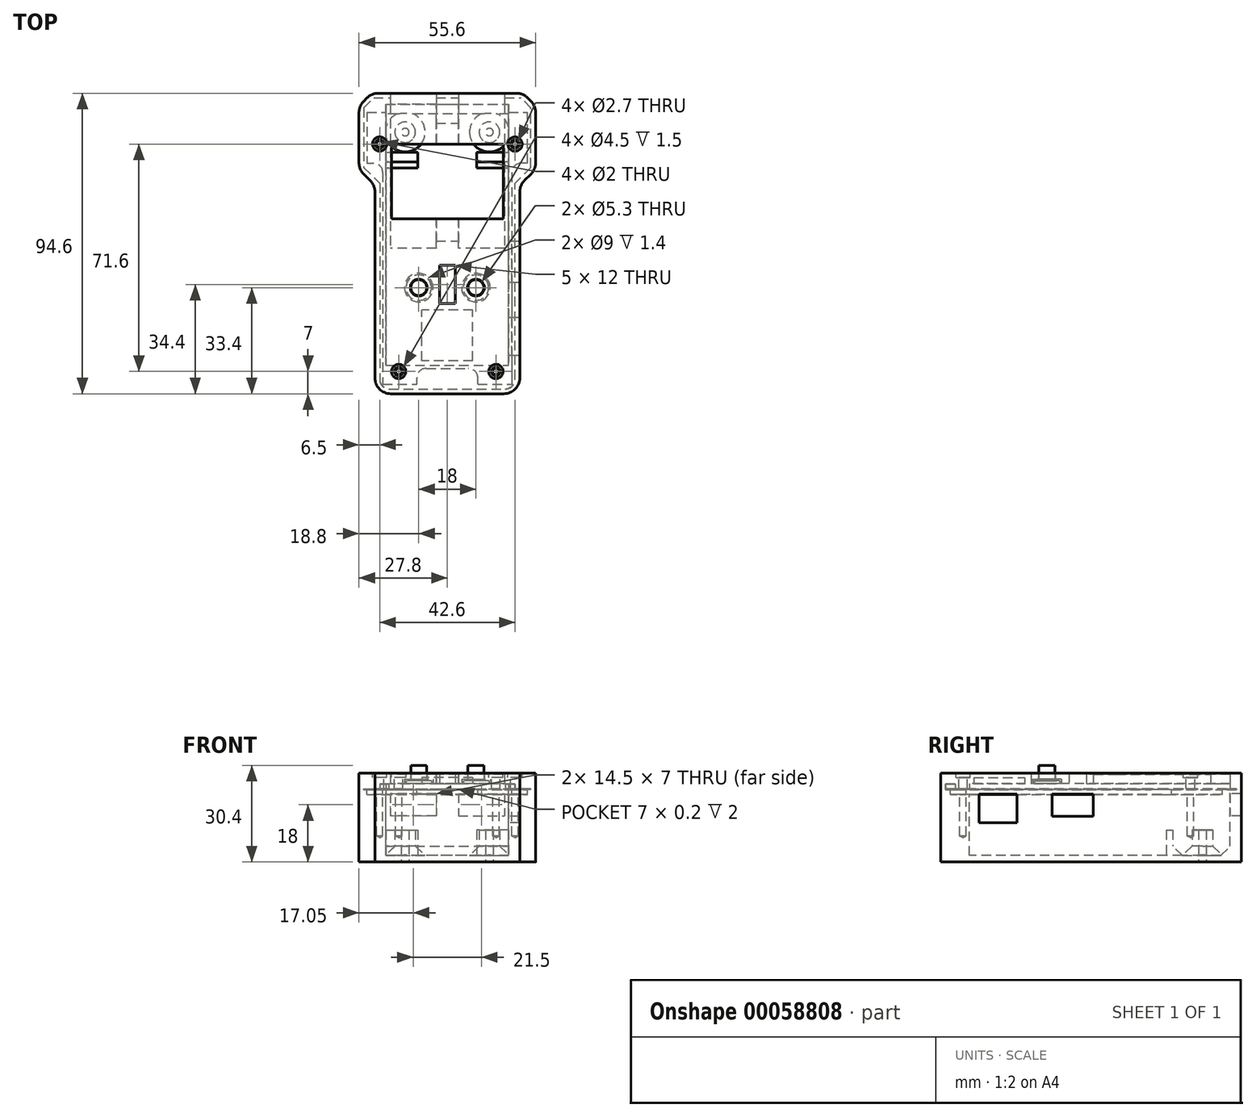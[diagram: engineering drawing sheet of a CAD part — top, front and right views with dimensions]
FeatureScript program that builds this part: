
annotation { "Feature Type Name" : "Feature", "Feature Type Description" : "" }
export const myFeature = defineFeature(function(context is Context, id is Id, definition is map)
    precondition{}
    {
        {
            assignVariable(context, id + "F0", {"name" : "GlassOffset", "anyValue" : 5.4});
        }
        {
            var Q0;
            Q0=qCreatedBy(makeId("Top.planeOp"),FACE);
            var sketch = newSketch(context, id + "F1", { "sketchPlane" : qUnion([Q0])});
            skLineSegment(sketch, "E0.rect.bottom", {"start": v(25.3, 42.8) * mm, "end": v(-25.3, 42.8) * mm, "construction": true});
            skLineSegment(sketch, "E0.rect.top", {"start": v(25.3, -42.8) * mm, "end": v(-25.3, -42.8) * mm, "construction": true});
            skLineSegment(sketch, "E0.rect.left", {"start": v(25.3, 42.8) * mm, "end": v(25.3, -42.8) * mm, "construction": true});
            skLineSegment(sketch, "E0.rect.right", {"start": v(-25.3, 42.8) * mm, "end": v(-25.3, -42.8) * mm, "construction": true});
            skPoint(sketch, "E0.rect.middle", {"position": v(0, 0) * mm});
            skLineSegment(sketch, "E1.rect.bottom", {"start": v(8, -35.4) * mm, "end": v(-8, -35.4) * mm});
            skLineSegment(sketch, "E1.rect.top", {"start": v(8, -19.4) * mm, "end": v(-8, -19.4) * mm});
            skLineSegment(sketch, "E1.rect.left", {"start": v(8, -35.4) * mm, "end": v(8, -19.4) * mm});
            skLineSegment(sketch, "E1.rect.right", {"start": v(-8, -35.4) * mm, "end": v(-8, -19.4) * mm});
            skPoint(sketch, "E1.rect.middle", {"position": v(0, -27.4) * mm});
            skPoint(sketch, "E2.rect.middle", {"position": v(0, 20.8) * mm});
            skLineSegment(sketch, "E3.rect.bottom", {"start": v(-5, -8.4) * mm, "end": v(-13, -8.4) * mm});
            skLineSegment(sketch, "E3.rect.top", {"start": v(-5, -16.4) * mm, "end": v(-13, -16.4) * mm});
            skLineSegment(sketch, "E3.rect.left", {"start": v(-5, -8.4) * mm, "end": v(-5, -16.4) * mm});
            skLineSegment(sketch, "E3.rect.right", {"start": v(-13, -8.4) * mm, "end": v(-13, -16.4) * mm});
            skPoint(sketch, "E3.rect.middle", {"position": v(-9, -12.4) * mm});
            skLineSegment(sketch, "E4.rect.bottom", {"start": v(13, -8.4) * mm, "end": v(5, -8.4) * mm});
            skLineSegment(sketch, "E4.rect.top", {"start": v(13, -16.4) * mm, "end": v(5, -16.4) * mm});
            skLineSegment(sketch, "E4.rect.left", {"start": v(13, -8.4) * mm, "end": v(13, -16.4) * mm});
            skLineSegment(sketch, "E4.rect.right", {"start": v(5, -8.4) * mm, "end": v(5, -16.4) * mm});
            skPoint(sketch, "E4.rect.middle", {"position": v(9, -12.4) * mm});
            skLineSegment(sketch, "E5", {"start": v(-9, -12.4) * mm, "end": v(9, -12.4) * mm, "construction": true});
            skLineSegment(sketch, "E6.rect.bottom", {"start": v(2.5, -5.4) * mm, "end": v(-2.5, -5.4) * mm});
            skLineSegment(sketch, "E6.rect.top", {"start": v(2.5, -17.4) * mm, "end": v(-2.5, -17.4) * mm});
            skLineSegment(sketch, "E6.rect.left", {"start": v(2.5, -5.4) * mm, "end": v(2.5, -17.4) * mm});
            skLineSegment(sketch, "E6.rect.right", {"start": v(-2.5, -5.4) * mm, "end": v(-2.5, -17.4) * mm});
            skPoint(sketch, "E6.rect.middle", {"position": v(0, -11.4) * mm});
            skCircle(sketch, "E7", {"center": v(-21.3, 32.8) * mm, "radius": 1.5 * mm});
            skCircle(sketch, "E8", {"center": v(21.3, 32.8) * mm, "radius": 1.5 * mm});
            skCircle(sketch, "E9", {"center": v(-15.3, -38.8) * mm, "radius": 1.5 * mm});
            skCircle(sketch, "E10", {"center": v(15.3, -38.8) * mm, "radius": 1.5 * mm});
            skLineSegment(sketch, "E11", {"start": v(18.3, -33.6) * mm, "end": v(18.3, -22.6) * mm, "construction": true});
            skLineSegment(sketch, "E12", {"start": v(16.3, -12.9) * mm, "end": v(16.3, 0.1) * mm, "construction": true});
            skPoint(sketch, "E13.visualSharp", {"position": v(16.3, 2.2) * mm});
            skArc(sketch, "E13.filletArc", {"start": v(17.8, 1.6) * mm, "mid": v(16.74, 1.16) * mm, "end": v(16.3, 0.1) * mm, "construction": true});
            skPoint(sketch, "E14.visualSharp", {"position": v(16.3, -10.8) * mm});
            skArc(sketch, "E14.filletArc", {"start": v(16.3, -12.9) * mm, "mid": v(16.74, -13.96) * mm, "end": v(17.8, -14.4) * mm, "construction": true});
            skPoint(sketch, "E15.visualSharp", {"position": v(18.3, -33.8) * mm});
            skArc(sketch, "E15.filletArc", {"start": v(18.3, -33.6) * mm, "mid": v(18.53, -34.17) * mm, "end": v(19.1, -34.4) * mm, "construction": true});
            skPoint(sketch, "E16.visualSharp", {"position": v(18.3, -21.8) * mm});
            skArc(sketch, "E16.filletArc", {"start": v(19.1, -21.8) * mm, "mid": v(18.53, -22.03) * mm, "end": v(18.3, -22.6) * mm, "construction": true});
            skLineSegment(sketch, "E17", {"start": v(-25.3, 42.8) * mm, "end": v(25.3, 42.8) * mm});
            skLineSegment(sketch, "E18", {"start": v(-25.3, 42.8) * mm, "end": v(-25.3, 26.8) * mm});
            skLineSegment(sketch, "E19", {"start": v(25.3, 26.8) * mm, "end": v(25.3, 42.8) * mm});
            skLineSegment(sketch, "E20", {"start": v(-25.3, 26.8) * mm, "end": v(-20.3, 26.8) * mm});
            skLineSegment(sketch, "E21", {"start": v(25.3, 26.8) * mm, "end": v(20.3, 26.8) * mm});
            skLineSegment(sketch, "E22", {"start": v(-20.3, 26.8) * mm, "end": v(-20.3, -42.8) * mm});
            skLineSegment(sketch, "E23", {"start": v(20.3, 26.8) * mm, "end": v(20.3, -42.8) * mm});
            skLineSegment(sketch, "E24", {"start": v(9.6, -42.8) * mm, "end": v(20.3, -42.8) * mm});
            skLineSegment(sketch, "E25", {"start": v(-9.6, -42.8) * mm, "end": v(-9.6, -37.8) * mm});
            skLineSegment(sketch, "E26", {"start": v(9.6, -42.8) * mm, "end": v(9.6, -37.8) * mm});
            skLineSegment(sketch, "E27", {"start": v(-20.3, -42.8) * mm, "end": v(-9.6, -42.8) * mm});
            skLineSegment(sketch, "E28", {"start": v(-9.6, -37.8) * mm, "end": v(9.6, -37.8) * mm});
            skLineSegment(sketch, "E29.rect.bottom", {"start": v(17.8, 39.3) * mm, "end": v(-17.8, 39.3) * mm});
            skLineSegment(sketch, "E29.rect.top", {"start": v(17.8, 2.3) * mm, "end": v(-17.8, 2.3) * mm});
            skLineSegment(sketch, "E29.rect.left", {"start": v(17.8, 39.3) * mm, "end": v(17.8, 2.3) * mm});
            skLineSegment(sketch, "E29.rect.right", {"start": v(-17.8, 39.3) * mm, "end": v(-17.8, 2.3) * mm});
            skLineSegment(sketch, "E30.rect.bottom", {"start": v(17.6, 9.3) * mm, "end": v(-17.6, 9.3) * mm});
            skLineSegment(sketch, "E30.rect.top", {"start": v(17.6, 32.8) * mm, "end": v(-17.6, 32.8) * mm});
            skLineSegment(sketch, "E30.rect.left", {"start": v(17.6, 9.3) * mm, "end": v(17.6, 32.8) * mm});
            skLineSegment(sketch, "E30.rect.right", {"start": v(-17.6, 9.3) * mm, "end": v(-17.6, 32.8) * mm});
            skPoint(sketch, "E30.rect.middle", {"position": v(0, 21.05) * mm});
            skLineSegment(sketch, "E31", {"start": v(0, 0) * mm, "end": v(0, 42.8) * mm, "construction": true});
            skLineSegment(sketch, "E32", {"start": v(0, 0) * mm, "end": v(0, -12.4) * mm, "construction": true});
            skCircle(sketch, "E33", {"center": v(-21.3, 32.8) * mm, "radius": 3 * mm});
            skCircle(sketch, "E34", {"center": v(21.3, 32.8) * mm, "radius": 3 * mm});
            skCircle(sketch, "E35", {"center": v(15.3, -38.8) * mm, "radius": 3 * mm});
            skCircle(sketch, "E36", {"center": v(-15.3, -38.8) * mm, "radius": 3 * mm});
            skLineSegment(sketch, "E37.MirrorCS", {"start": v(18.9, 40.8) * mm, "end": v(3.9, 40.8) * mm, "construction": true});
            skSolve(sketch);
        }
        {
            var Q0;
            Q0=qCreatedBy(makeId("Top.planeOp"),FACE);
            var sketch = newSketch(context, id + "F2", { "sketchPlane" : qUnion([Q0])});
            skPoint(sketch, "E38.0", {"position": v(-9, -12.4) * mm});
            skPoint(sketch, "E39.0", {"position": v(9, -12.4) * mm});
            skCircle(sketch, "E40", {"center": v(-9, -12.4) * mm, "radius": 4 * mm});
            skCircle(sketch, "E41", {"center": v(9, -12.4) * mm, "radius": 4 * mm});
            skCircle(sketch, "E42", {"center": v(-9, -12.4) * mm, "radius": 2.5 * mm});
            skCircle(sketch, "E43", {"center": v(9, -12.4) * mm, "radius": 2.5 * mm});
            skSolve(sketch);
        }
        {
            var Q0;
            Q0=qCreatedBy(makeId("Top.planeOp"),FACE);
            var sketch = newSketch(context, id + "F3", { "sketchPlane" : qUnion([Q0])});
            skLineSegment(sketch, "E44", {"start": v(-22.8, -45.8) * mm, "end": v(22.8, -45.8) * mm});
            skLineSegment(sketch, "E45", {"start": v(-27.8, 24.8) * mm, "end": v(-22.8, 19.8) * mm});
            skLineSegment(sketch, "E46", {"start": v(-22.8, 19.8) * mm, "end": v(-22.8, -45.8) * mm});
            skLineSegment(sketch, "E47", {"start": v(27.8, 24.8) * mm, "end": v(22.8, 19.8) * mm});
            skLineSegment(sketch, "E48", {"start": v(22.8, -45.8) * mm, "end": v(22.8, 19.8) * mm});
            skLineSegment(sketch, "E49", {"start": v(-27.8, 44.8) * mm, "end": v(-23.8, 48.8) * mm});
            skLineSegment(sketch, "E50", {"start": v(27.8, 44.8) * mm, "end": v(23.8, 48.8) * mm});
            skLineSegment(sketch, "E51", {"start": v(-27.8, 44.8) * mm, "end": v(-27.8, 24.8) * mm});
            skLineSegment(sketch, "E52", {"start": v(27.8, 24.8) * mm, "end": v(27.8, 44.8) * mm});
            skLineSegment(sketch, "E53", {"start": v(-23.8, 48.8) * mm, "end": v(23.8, 48.8) * mm});
            skLineSegment(sketch, "E54.0", {"start": v(-26.3, 44.18) * mm, "end": v(-23.18, 47.3) * mm});
            skLineSegment(sketch, "E54.1", {"start": v(-23.18, 47.3) * mm, "end": v(23.18, 47.3) * mm});
            skLineSegment(sketch, "E54.2", {"start": v(-26.3, 44.18) * mm, "end": v(-26.3, 25.42) * mm});
            skLineSegment(sketch, "E54.3", {"start": v(26.3, 44.18) * mm, "end": v(23.18, 47.3) * mm});
            skLineSegment(sketch, "E54.4", {"start": v(26.3, 25.42) * mm, "end": v(26.3, 44.18) * mm});
            skLineSegment(sketch, "E54.5", {"start": v(26.3, 25.42) * mm, "end": v(21.3, 20.42) * mm});
            skLineSegment(sketch, "E54.6", {"start": v(-26.3, 25.42) * mm, "end": v(-21.3, 20.42) * mm});
            skLineSegment(sketch, "E54.7", {"start": v(-21.3, 20.42) * mm, "end": v(-21.3, -44.3) * mm});
            skLineSegment(sketch, "E54.8", {"start": v(-21.3, -44.3) * mm, "end": v(21.3, -44.3) * mm});
            skLineSegment(sketch, "E54.9", {"start": v(21.3, -44.3) * mm, "end": v(21.3, 20.42) * mm});
            skLineSegment(sketch, "E55", {"start": v(-19.3, -36.8) * mm, "end": v(19.3, -36.8) * mm});
            skLineSegment(sketch, "E56", {"start": v(-19.3, -36.8) * mm, "end": v(-19.3, 45.3) * mm});
            skLineSegment(sketch, "E57", {"start": v(-19.3, 45.3) * mm, "end": v(19.3, 45.3) * mm});
            skLineSegment(sketch, "E58", {"start": v(19.3, 45.3) * mm, "end": v(19.3, -36.8) * mm});
            skSolve(sketch);
        }
        {
            var Q0;
            Q0=qCreatedBy(makeId("Front.planeOp"),FACE);
            var sketch = newSketch(context, id + "F4", { "sketchPlane" : qUnion([Q0])});
            skLineSegment(sketch, "E59.bottom", {"start": v(-3.5, -1.5) * mm, "end": v(-18, -1.5) * mm});
            skLineSegment(sketch, "E59.top", {"start": v(-3.5, -8.5) * mm, "end": v(-18, -8.5) * mm});
            skLineSegment(sketch, "E59.left", {"start": v(-3.5, -1.5) * mm, "end": v(-3.5, -8.5) * mm});
            skLineSegment(sketch, "E59.right", {"start": v(-18, -1.5) * mm, "end": v(-18, -8.5) * mm});
            skLineSegment(sketch, "E60.MirrorCS", {"start": v(3.5, -1.5) * mm, "end": v(18, -1.5) * mm});
            skLineSegment(sketch, "E61.MirrorCS", {"start": v(18, -1.5) * mm, "end": v(18, -8.5) * mm});
            skLineSegment(sketch, "E62.MirrorCS", {"start": v(3.5, -8.5) * mm, "end": v(18, -8.5) * mm});
            skLineSegment(sketch, "E63.MirrorCS", {"start": v(3.5, -1.5) * mm, "end": v(3.5, -8.5) * mm});
            skLineSegment(sketch, "E64", {"start": v(-3.5, -1.5) * mm, "end": v(-3.5, 4.64) * mm});
            skLineSegment(sketch, "E65", {"start": v(-3.5, 4.64) * mm, "end": v(-18, 4.64) * mm});
            skLineSegment(sketch, "E66", {"start": v(-18, 4.64) * mm, "end": v(-18, -1.5) * mm});
            skLineSegment(sketch, "E67", {"start": v(18, -1.5) * mm, "end": v(18, 4.64) * mm});
            skLineSegment(sketch, "E68", {"start": v(18, 4.64) * mm, "end": v(3.5, 4.64) * mm});
            skLineSegment(sketch, "E69", {"start": v(3.5, 4.64) * mm, "end": v(3.5, -1.5) * mm});
            skSolve(sketch);
        }
        {
            var Q0;
            Q0=qCreatedBy(makeId("Right.planeOp"),FACE);
            var sketch = newSketch(context, id + "F5", { "sketchPlane" : qUnion([Q0])});
            skLineSegment(sketch, "E70.bottom", {"start": v(-33.8, -1.6) * mm, "end": v(-21.8, -1.6) * mm});
            skLineSegment(sketch, "E70.top", {"start": v(-33.8, -10.6) * mm, "end": v(-21.8, -10.6) * mm});
            skLineSegment(sketch, "E70.left", {"start": v(-33.8, -1.6) * mm, "end": v(-33.8, -10.6) * mm});
            skLineSegment(sketch, "E70.right", {"start": v(-21.8, -1.6) * mm, "end": v(-21.8, -10.6) * mm});
            skLineSegment(sketch, "E71.bottom", {"start": v(-10.8, -1.6) * mm, "end": v(2.2, -1.6) * mm});
            skLineSegment(sketch, "E71.top", {"start": v(-10.8, -8.6) * mm, "end": v(2.2, -8.6) * mm});
            skLineSegment(sketch, "E71.left", {"start": v(-10.8, -1.6) * mm, "end": v(-10.8, -8.6) * mm});
            skLineSegment(sketch, "E71.right", {"start": v(2.2, -1.6) * mm, "end": v(2.2, -8.6) * mm});
            skPoint(sketch, "E72.0", {"position": v(-33.8, 0) * mm});
            skPoint(sketch, "E73.0", {"position": v(-21.8, 0) * mm});
            skPoint(sketch, "E74.0", {"position": v(-10.8, 0) * mm});
            skPoint(sketch, "E75.0", {"position": v(2.2, 0) * mm});
            skSolve(sketch);
        }
        {
            var Q0;
            Q0=makeQuery(id+"F3.imprint","IMPRINT",FACE,{"disambiguationData":[TD([[makeQuery(id+"F3.imprint","IMPRINT",EDGE,{"derivedFrom":sQuery(id+"F3.wireOp",EDGE,"daaaa8a0-0a0e-469a-a0b3-6c36c1fbd0ea.6")}),1.0]])]});
            var Q1;
            Q1=makeQuery(id+"F3.imprint","IMPRINT",FACE,{"disambiguationData":[TD([[makeQuery(id+"F3.imprint","IMPRINT",EDGE,{"derivedFrom":sQuery(id+"F3.wireOp",EDGE,"E44")}),1.0]])]});
            var Q2;
            Q2=makeQuery(id+"F3.imprint","IMPRINT",FACE,{"disambiguationData":[TD([[makeQuery(id+"F3.imprint","IMPRINT",EDGE,{"derivedFrom":sQuery(id+"F3.wireOp",EDGE,"E54.0")}),-1.0]])]});
            var Q3;
            Q3=makeQuery(id+"F3.imprint","IMPRINT",FACE,{"disambiguationData":[TD([[makeQuery(id+"F3.imprint","IMPRINT",EDGE,{"derivedFrom":sQuery(id+"F3.wireOp",EDGE,"E55")}),1.0]])]});
            extrude(context, id + "F6", {"entities" : qUnion([Q0, Q1, Q2, Q3]), "depth" : 5 * mm});
        }
        {
            var Q0;
            Q0=makeQuery(id+"F3.imprint","IMPRINT",FACE,{"disambiguationData":[TD([[makeQuery(id+"F3.imprint","IMPRINT",EDGE,{"derivedFrom":sQuery(id+"F3.wireOp",EDGE,"E44")}),1.0]])]});
            extrude(context, id + "F7", {"entities" : qUnion([Q0]), "operationType" : NewBodyOperationType.REMOVE, "depth" : 1.5 * mm});
        }
        {
            var Q0;
            Q0=makeQuery(id+"F3.imprint","IMPRINT",FACE,{"disambiguationData":[TD([[makeQuery(id+"F3.imprint","IMPRINT",EDGE,{"derivedFrom":sQuery(id+"F3.wireOp",EDGE,"E44")}),1.0]])]});
            extrude(context, id + "F8", {"entities" : qUnion([Q0]), "oppositeDirection" : true, "depth" : 23 * mm, "hasSecondDirection" : true, "secondDirectionOppositeDirection" : false, "secondDirectionDepth" : 1.5 * mm});
        }
        {
            var Q0;
            Q0=makeQuery(id+"F3.imprint","IMPRINT",FACE,{"disambiguationData":[TD([[makeQuery(id+"F3.imprint","IMPRINT",EDGE,{"derivedFrom":sQuery(id+"F3.wireOp",EDGE,"E54.0")}),-1.0]])]});
            var Q1;
            Q1=makeQuery(id+"F8.opExtrude","CAP_FACE",FACE,{"disambiguationData":[OSD([sQuery(id+"F3.wireOp",EDGE,"E44"),sQuery(id+"F3.wireOp",EDGE,"E45"),sQuery(id+"F3.wireOp",EDGE,"E46"),sQuery(id+"F3.wireOp",EDGE,"E47"),sQuery(id+"F3.wireOp",EDGE,"E48"),sQuery(id+"F3.wireOp",EDGE,"E49"),sQuery(id+"F3.wireOp",EDGE,"E50"),sQuery(id+"F3.wireOp",EDGE,"E51"),sQuery(id+"F3.wireOp",EDGE,"E52"),sQuery(id+"F3.wireOp",EDGE,"E53"),sQuery(id+"F3.wireOp",EDGE,"E54.0"),sQuery(id+"F3.wireOp",EDGE,"E54.1"),sQuery(id+"F3.wireOp",EDGE,"E54.2"),sQuery(id+"F3.wireOp",EDGE,"E54.3"),sQuery(id+"F3.wireOp",EDGE,"E54.4"),sQuery(id+"F3.wireOp",EDGE,"E54.5"),sQuery(id+"F3.wireOp",EDGE,"E54.6"),sQuery(id+"F3.wireOp",EDGE,"E54.7"),sQuery(id+"F3.wireOp",EDGE,"E54.8"),sQuery(id+"F3.wireOp",EDGE,"E54.9")])],"isStart":false});
            extrude(context, id + "F9", {"entities" : qUnion([Q0]), "operationType" : NewBodyOperationType.ADD, "endBound" : BoundingType.UP_TO_SURFACE, "oppositeDirection" : true, "endBoundEntityFace" : qUnion([Q1]), "depth" : 5 * mm, "hasSecondDirection" : true, "secondDirectionOppositeDirection" : true, "secondDirectionDepth" : .2 * mm});
        }
        {
            var Q0;
            Q0=makeQuery(id+"F1.imprint","IMPRINT",FACE,{"disambiguationData":[TD([[makeQuery(id+"F1.imprint","IMPRINT",EDGE,{"derivedFrom":sQuery(id+"F1.wireOp",EDGE,"E30.rect.bottom")}),-1.0]])]});
            var Q1;
            Q1=makeQuery(id+"F1.imprint","IMPRINT",FACE,{"disambiguationData":[TD([[makeQuery(id+"F1.imprint","IMPRINT",EDGE,{"derivedFrom":sQuery(id+"F1.wireOp",EDGE,"E6.rect.bottom")}),1.0]])]});
            extrude(context, id + "F10", {"entities" : qUnion([Q0, Q1]), "operationType" : NewBodyOperationType.REMOVE, "depth" : 25 * mm});
        }
        {
            var Q0;
            Q0=sQuery(id+"F1.wireOp",VERTEX,"E3.rect.middle");
            var Q1;
            Q1=sQuery(id+"F1.wireOp",VERTEX,"E4.rect.middle");
            var Q2;
            Q2=makeQuery(id+"F6.opExtrude","SWEPT_BODY",BODY,{"disambiguationData":[OSD([sQuery(id+"F3.wireOp",EDGE,"E44"),sQuery(id+"F3.wireOp",EDGE,"E45"),sQuery(id+"F3.wireOp",EDGE,"E46"),sQuery(id+"F3.wireOp",EDGE,"E47"),sQuery(id+"F3.wireOp",EDGE,"E48"),sQuery(id+"F3.wireOp",EDGE,"E49"),sQuery(id+"F3.wireOp",EDGE,"E50"),sQuery(id+"F3.wireOp",EDGE,"E51"),sQuery(id+"F3.wireOp",EDGE,"E52"),sQuery(id+"F3.wireOp",EDGE,"E53"),sQuery(id+"F3.wireOp",EDGE,"E55"),sQuery(id+"F3.wireOp",EDGE,"E56"),sQuery(id+"F3.wireOp",EDGE,"E57"),sQuery(id+"F3.wireOp",EDGE,"E58")])]});
            hole(context, id + "F11", {"style" : HoleStyle.C_BORE, "endStyle" : HoleEndStyle.BLIND, "oppositeDirection" : true, "holeDiameter" : 5.3 * mm, "cBoreDiameter" : 9 * mm, "cBoreDepth" : 3.1 * mm, "holeDepth" : 7 * mm, "locations" : qUnion([Q0, Q1]), "scope" : qUnion([Q2])});
        }
        {
            var Q0;
            Q0 = qSketchRegion(id + "F2", true);
            extrude(context, id + "F12", {"entities" : qUnion([Q0]), "depth" : 2.6 * mm, "hasSecondDirection" : true, "secondDirectionOppositeDirection" : false, "secondDirectionDepth" : 1.6 * mm});
        }
        {
            var Q0;
            Q0=makeQuery(id+"F2.imprint","IMPRINT",FACE,{"disambiguationData":[TD([[makeQuery(id+"F2.imprint","IMPRINT",EDGE,{"derivedFrom":sQuery(id+"F2.wireOp",EDGE,"E42")}),1.0]])]});
            var Q1;
            Q1=makeQuery(id+"F2.imprint","IMPRINT",FACE,{"disambiguationData":[TD([[makeQuery(id+"F2.imprint","IMPRINT",EDGE,{"derivedFrom":sQuery(id+"F2.wireOp",EDGE,"E43")}),1.0]])]});
            var Q2;
            Q2=sQuery(id+"F2.wireOp",EDGE,"E42");
            var Q3;
            Q3=sQuery(id+"F2.wireOp",EDGE,"E43");
            extrude(context, id + "F13", {"entities" : qUnion([Q0, Q1]), "operationType" : NewBodyOperationType.ADD, "surfaceEntities" : qUnion([Q2, Q3]), "depth" : (getVariable(context, 'GlassOffset') + 2) * mm, "hasSecondDirection" : true, "secondDirectionOppositeDirection" : false, "secondDirectionDepth" : 1.6 * mm});
        }
        {
            var Q0;
            Q0=makeQuery(id+"F1.imprint","IMPRINT",FACE,{"disambiguationData":[TD([[makeQuery(id+"F1.imprint","IMPRINT",EDGE,{"derivedFrom":sQuery(id+"F1.wireOp",EDGE,"E1.rect.bottom")}),1.0]])]});
            var Q1;
            Q1=makeQuery(id+"F1.imprint","IMPRINT",FACE,{"disambiguationData":[TD([[makeQuery(id+"F1.imprint","IMPRINT",EDGE,{"derivedFrom":sQuery(id+"F1.wireOp",EDGE,"E7")}),-1.0]])]});
            var Q2;
            Q2=makeQuery(id+"F1.imprint","IMPRINT",FACE,{"disambiguationData":[TD([[makeQuery(id+"F1.imprint","IMPRINT",EDGE,{"derivedFrom":sQuery(id+"F1.wireOp",EDGE,"E7")}),1.0]])]});
            var Q3;
            Q3=makeQuery(id+"F1.imprint","IMPRINT",FACE,{"disambiguationData":[TD([[makeQuery(id+"F1.imprint","IMPRINT",EDGE,{"derivedFrom":sQuery(id+"F1.wireOp",EDGE,"E8")}),-1.0]])]});
            var Q4;
            Q4=makeQuery(id+"F1.imprint","IMPRINT",FACE,{"disambiguationData":[TD([[makeQuery(id+"F1.imprint","IMPRINT",EDGE,{"derivedFrom":sQuery(id+"F1.wireOp",EDGE,"E8")}),1.0]])]});
            var Q5;
            Q5=makeQuery(id+"F1.imprint","IMPRINT",FACE,{"disambiguationData":[TD([[makeQuery(id+"F1.imprint","IMPRINT",EDGE,{"derivedFrom":sQuery(id+"F1.wireOp",EDGE,"E10")}),-1.0]])]});
            var Q6;
            Q6=makeQuery(id+"F1.imprint","IMPRINT",FACE,{"disambiguationData":[TD([[makeQuery(id+"F1.imprint","IMPRINT",EDGE,{"derivedFrom":sQuery(id+"F1.wireOp",EDGE,"E10")}),1.0]])]});
            var Q7;
            Q7=makeQuery(id+"F1.imprint","IMPRINT",FACE,{"disambiguationData":[TD([[makeQuery(id+"F1.imprint","IMPRINT",EDGE,{"derivedFrom":sQuery(id+"F1.wireOp",EDGE,"E9")}),-1.0]])]});
            var Q8;
            Q8=makeQuery(id+"F1.imprint","IMPRINT",FACE,{"disambiguationData":[TD([[makeQuery(id+"F1.imprint","IMPRINT",EDGE,{"derivedFrom":sQuery(id+"F1.wireOp",EDGE,"E9")}),1.0]])]});
            extrude(context, id + "F14", {"entities" : qUnion([Q0, Q1, Q2, Q3, Q4, Q5, Q6, Q7, Q8]), "operationType" : NewBodyOperationType.REMOVE, "oppositeDirection" : true, "depth" : 1.8 * mm});
        }
        {
            var Q0;
            Q0=makeQuery(id+"F14.boolean.opBoolean","COPY",EDGE,{"derivedFrom":makeQuery(id+"F14.opExtrude","SWEPT_EDGE",EDGE,{"disambiguationData":[OSD([sQuery(id+"F1.wireOp",EDGE,"E21"),sQuery(id+"F1.wireOp",EDGE,"E23")])]})});
            var Q1;
            Q1=makeQuery(id+"F14.boolean.opBoolean","COPY",EDGE,{"derivedFrom":makeQuery(id+"F14.opExtrude","SWEPT_EDGE",EDGE,{"disambiguationData":[OSD([sQuery(id+"F1.wireOp",EDGE,"E26"),sQuery(id+"F1.wireOp",EDGE,"E28")])]})});
            var Q2;
            Q2=makeQuery(id+"F14.boolean.opBoolean","COPY",EDGE,{"derivedFrom":makeQuery(id+"F14.opExtrude","SWEPT_EDGE",EDGE,{"disambiguationData":[OSD([sQuery(id+"F1.wireOp",EDGE,"E25"),sQuery(id+"F1.wireOp",EDGE,"E28")])]})});
            var Q3;
            Q3=makeQuery(id+"F14.boolean.opBoolean","COPY",EDGE,{"derivedFrom":makeQuery(id+"F14.opExtrude","SWEPT_EDGE",EDGE,{"disambiguationData":[OSD([sQuery(id+"F1.wireOp",EDGE,"E20"),sQuery(id+"F1.wireOp",EDGE,"E22")])]})});
            fillet(context, id + "F15", {"entities" : qUnion([Q0, Q1, Q2, Q3]), "radius" : 3 * mm, "tangentPropagation" : true, "allowEdgeOverflow" : false});
        }
        {
            var Q0;
            Q0=makeQuery(id+"F4.imprint","IMPRINT",FACE,{"disambiguationData":[TD([[makeQuery(id+"F4.imprint","IMPRINT",EDGE,{"derivedFrom":sQuery(id+"F4.wireOp",EDGE,"E59.bottom")}),1.0]])]});
            var Q1;
            Q1=makeQuery(id+"F4.imprint","IMPRINT",FACE,{"disambiguationData":[TD([[makeQuery(id+"F4.imprint","IMPRINT",EDGE,{"derivedFrom":sQuery(id+"F4.wireOp",EDGE,"E60.MirrorCS")}),-1.0]])]});
            var Q2;
            Q2=makeQuery(id+"F4.imprint","IMPRINT",FACE,{"disambiguationData":[TD([[makeQuery(id+"F4.imprint","IMPRINT",EDGE,{"derivedFrom":sQuery(id+"F4.wireOp",EDGE,"E60.MirrorCS")}),1.0]])]});
            var Q3;
            Q3=makeQuery(id+"F4.imprint","IMPRINT",FACE,{"disambiguationData":[TD([[makeQuery(id+"F4.imprint","IMPRINT",EDGE,{"derivedFrom":sQuery(id+"F4.wireOp",EDGE,"E59.bottom")}),-1.0]])]});
            extrude(context, id + "F16", {"entities" : qUnion([Q0, Q1, Q2, Q3]), "operationType" : NewBodyOperationType.REMOVE, "oppositeDirection" : true, "depth" : 50 * mm});
        }
        {
            var Q0;
            Q0=makeQuery(id+"F5.imprint","IMPRINT",FACE,{"disambiguationData":[TD([[makeQuery(id+"F5.imprint","IMPRINT",EDGE,{"derivedFrom":sQuery(id+"F5.wireOp",EDGE,"E70.bottom")}),-1.0]])]});
            var Q1;
            Q1=makeQuery(id+"F5.imprint","IMPRINT",FACE,{"disambiguationData":[TD([[makeQuery(id+"F5.imprint","IMPRINT",EDGE,{"derivedFrom":sQuery(id+"F5.wireOp",EDGE,"E71.bottom")}),-1.0]])]});
            extrude(context, id + "F17", {"entities" : qUnion([Q0, Q1]), "operationType" : NewBodyOperationType.REMOVE, "depth" : 25 * mm});
        }
        {
            var Q0;
            Q0=makeQuery(id+"F3.imprint","IMPRINT",FACE,{"disambiguationData":[TD([[makeQuery(id+"F3.imprint","IMPRINT",EDGE,{"derivedFrom":sQuery(id+"F3.wireOp",EDGE,"E44")}),1.0]])]});
            var Q1;
            Q1=makeQuery(id+"F3.imprint","IMPRINT",FACE,{"disambiguationData":[TD([[makeQuery(id+"F3.imprint","IMPRINT",EDGE,{"derivedFrom":sQuery(id+"F3.wireOp",EDGE,"E54.0")}),-1.0]])]});
            var Q2;
            Q2=makeQuery(id+"F3.imprint","IMPRINT",FACE,{"disambiguationData":[TD([[makeQuery(id+"F3.imprint","IMPRINT",EDGE,{"derivedFrom":sQuery(id+"F3.wireOp",EDGE,"E55")}),1.0]])]});
            var Q3;
            {var subQ0=sQuery(id+"F3.wireOp",EDGE,"E54.9");var subQ1=sQuery(id+"F3.wireOp",EDGE,"E54.8");var subQ2=sQuery(id+"F3.wireOp",EDGE,"E54.7");var subQ3=sQuery(id+"F3.wireOp",EDGE,"E54.6");var subQ4=sQuery(id+"F3.wireOp",EDGE,"E54.5");var subQ5=sQuery(id+"F3.wireOp",EDGE,"E54.4");var subQ6=sQuery(id+"F3.wireOp",EDGE,"E54.3");var subQ7=sQuery(id+"F3.wireOp",EDGE,"E54.2");var subQ8=sQuery(id+"F3.wireOp",EDGE,"E54.1");var subQ9=sQuery(id+"F3.wireOp",EDGE,"E54.0");var subQ10=sQuery(id+"F3.wireOp",EDGE,"E53");var subQ11=sQuery(id+"F3.wireOp",EDGE,"E52");var subQ12=sQuery(id+"F3.wireOp",EDGE,"E51");var subQ13=sQuery(id+"F3.wireOp",EDGE,"E50");var subQ14=sQuery(id+"F3.wireOp",EDGE,"E49");var subQ15=sQuery(id+"F3.wireOp",EDGE,"E48");var subQ16=sQuery(id+"F3.wireOp",EDGE,"E47");var subQ17=sQuery(id+"F3.wireOp",EDGE,"E46");var subQ18=sQuery(id+"F3.wireOp",EDGE,"E45");var subQ19=sQuery(id+"F3.wireOp",EDGE,"E44");Q3=makeQuery(id+"F9.boolean.opBoolean","MERGE",FACE,{"derivedFrom":[makeQuery(id+"F8.opExtrude","CAP_FACE",FACE,{"disambiguationData":[OSD([subQ19,subQ18,subQ17,subQ16,subQ15,subQ14,subQ13,subQ12,subQ11,subQ10,subQ9,subQ8,subQ7,subQ6,subQ5,subQ4,subQ3,subQ2,subQ1,subQ0])],"isStart":false}),makeQuery(id+"F9.opExtrude","CAP_FACE",FACE,{"disambiguationData":[OSD([subQ19,subQ18,subQ17,subQ16,subQ15,subQ14,subQ13,subQ12,subQ11,subQ10,subQ9,subQ8,subQ7,subQ6,subQ5,subQ4,subQ3,subQ2,subQ1,subQ0])],"isStart":false})]});}
            extrude(context, id + "F18", {"entities" : qUnion([Q0, Q1, Q2]), "operationType" : NewBodyOperationType.ADD, "endBound" : BoundingType.UP_TO_SURFACE, "oppositeDirection" : true, "endBoundEntityFace" : qUnion([Q3]), "depth" : 25 * mm, "hasSecondDirection" : true, "secondDirectionOppositeDirection" : true, "secondDirectionDepth" : 21 * mm});
        }
        {
            var Q0;
            Q0=makeQuery(id+"F1.imprint","IMPRINT",FACE,{"disambiguationData":[TD([[makeQuery(id+"F1.imprint","IMPRINT",EDGE,{"derivedFrom":sQuery(id+"F1.wireOp",EDGE,"E1.rect.bottom")}),-1.0]])]});
            extrude(context, id + "F19", {"entities" : qUnion([Q0]), "operationType" : NewBodyOperationType.REMOVE, "depth" : 3.5 * mm});
        }
        {
            var Q0;
            Q0=makeQuery(id+"F1.imprint","IMPRINT",FACE,{"disambiguationData":[TD([[makeQuery(id+"F1.imprint","IMPRINT",EDGE,{"derivedFrom":sQuery(id+"F1.wireOp",EDGE,"E3.rect.bottom")}),1.0]])]});
            var Q1;
            Q1=makeQuery(id+"F1.imprint","IMPRINT",FACE,{"disambiguationData":[TD([[makeQuery(id+"F1.imprint","IMPRINT",EDGE,{"derivedFrom":sQuery(id+"F1.wireOp",EDGE,"E4.rect.bottom")}),1.0]])]});
            var Q2;
            Q2=makeQuery(id+"F3.imprint","IMPRINT",FACE,{"disambiguationData":[TD([[makeQuery(id+"F3.imprint","IMPRINT",EDGE,{"derivedFrom":sQuery(id+"F3.wireOp",EDGE,"E55")}),1.0]])]});
            extrude(context, id + "F20", {"entities" : qUnion([Q0, Q1, Q2]), "operationType" : NewBodyOperationType.REMOVE, "depth" : 1.7 * mm});
        }
        {
            var Q0;
            Q0=makeQuery(id+"F1.imprint","IMPRINT",FACE,{"disambiguationData":[TD([[makeQuery(id+"F1.imprint","IMPRINT",EDGE,{"derivedFrom":sQuery(id+"F1.wireOp",EDGE,"E29.rect.bottom")}),1.0]])]});
            extrude(context, id + "F21", {"entities" : qUnion([Q0]), "operationType" : NewBodyOperationType.REMOVE, "depth" : (getVariable(context, 'GlassOffset') - .8) * mm});
        }
        {
            var Q0;
            Q0=makeQuery(id+"F6.opExtrude","CAP_FACE",FACE,{"disambiguationData":[OSD([sQuery(id+"F3.wireOp",EDGE,"E44"),sQuery(id+"F3.wireOp",EDGE,"E45"),sQuery(id+"F3.wireOp",EDGE,"E46"),sQuery(id+"F3.wireOp",EDGE,"E47"),sQuery(id+"F3.wireOp",EDGE,"E48"),sQuery(id+"F3.wireOp",EDGE,"E49"),sQuery(id+"F3.wireOp",EDGE,"E50"),sQuery(id+"F3.wireOp",EDGE,"E51"),sQuery(id+"F3.wireOp",EDGE,"E52"),sQuery(id+"F3.wireOp",EDGE,"E53")])],"isStart":false});
            var sketch = newSketch(context, id + "F22", { "sketchPlane" : qUnion([Q0])});
            skPoint(sketch, "E76.0", {"position": v(-21.3, 32.8) * mm});
            skPoint(sketch, "E77.0", {"position": v(21.3, 32.8) * mm});
            skPoint(sketch, "E78.0", {"position": v(15.3, -38.8) * mm});
            skPoint(sketch, "E79.0", {"position": v(-15.3, -38.8) * mm});
            skSolve(sketch);
        }
        {
            var Q0;
            Q0=sQuery(id+"F22.wireOp",VERTEX,"E79.0");
            var Q1;
            Q1=sQuery(id+"F22.wireOp",VERTEX,"E78.0");
            var Q2;
            Q2=sQuery(id+"F22.wireOp",VERTEX,"E76.0");
            var Q3;
            Q3=sQuery(id+"F22.wireOp",VERTEX,"E77.0");
            var Q4;
            Q4=makeQuery(id+"F6.opExtrude","SWEPT_BODY",BODY,{"disambiguationData":[OSD([sQuery(id+"F3.wireOp",EDGE,"E44"),sQuery(id+"F3.wireOp",EDGE,"E45"),sQuery(id+"F3.wireOp",EDGE,"E46"),sQuery(id+"F3.wireOp",EDGE,"E47"),sQuery(id+"F3.wireOp",EDGE,"E48"),sQuery(id+"F3.wireOp",EDGE,"E49"),sQuery(id+"F3.wireOp",EDGE,"E50"),sQuery(id+"F3.wireOp",EDGE,"E51"),sQuery(id+"F3.wireOp",EDGE,"E52"),sQuery(id+"F3.wireOp",EDGE,"E53")])]});
            var Q5;
            Q5=makeQuery(id+"F8.opExtrude","SWEPT_BODY",BODY,{"disambiguationData":[OSD([sQuery(id+"F3.wireOp",EDGE,"E44"),sQuery(id+"F3.wireOp",EDGE,"E45"),sQuery(id+"F3.wireOp",EDGE,"E46"),sQuery(id+"F3.wireOp",EDGE,"E47"),sQuery(id+"F3.wireOp",EDGE,"E48"),sQuery(id+"F3.wireOp",EDGE,"E49"),sQuery(id+"F3.wireOp",EDGE,"E50"),sQuery(id+"F3.wireOp",EDGE,"E51"),sQuery(id+"F3.wireOp",EDGE,"E52"),sQuery(id+"F3.wireOp",EDGE,"E53"),sQuery(id+"F3.wireOp",EDGE,"E54.0"),sQuery(id+"F3.wireOp",EDGE,"E54.1"),sQuery(id+"F3.wireOp",EDGE,"E54.2"),sQuery(id+"F3.wireOp",EDGE,"E54.3"),sQuery(id+"F3.wireOp",EDGE,"E54.4"),sQuery(id+"F3.wireOp",EDGE,"E54.5"),sQuery(id+"F3.wireOp",EDGE,"E54.6"),sQuery(id+"F3.wireOp",EDGE,"E54.7"),sQuery(id+"F3.wireOp",EDGE,"E54.8"),sQuery(id+"F3.wireOp",EDGE,"E54.9")])]});
            hole(context, id + "F23", {"style" : HoleStyle.C_BORE, "endStyle" : HoleEndStyle.BLIND_IN_LAST, "holeDiameter" : 2.7 * mm, "cBoreDiameter" : 4.5 * mm, "cBoreDepth" : 1.5 * mm, "tapDrillDiameter" : 2 * mm, "holeDepth" : 13 * mm, "locations" : qUnion([Q0, Q1, Q2, Q3]), "scope" : qUnion([Q4, Q5])});
        }
        {
            var Q0;
            {var subQ0=sQuery(id+"F3.wireOp",EDGE,"E54.9");var subQ1=sQuery(id+"F3.wireOp",EDGE,"E54.8");var subQ2=sQuery(id+"F3.wireOp",EDGE,"E54.7");var subQ3=sQuery(id+"F3.wireOp",EDGE,"E54.6");var subQ4=sQuery(id+"F3.wireOp",EDGE,"E54.5");var subQ5=sQuery(id+"F3.wireOp",EDGE,"E54.4");var subQ6=sQuery(id+"F3.wireOp",EDGE,"E54.3");var subQ7=sQuery(id+"F3.wireOp",EDGE,"E54.2");var subQ8=sQuery(id+"F3.wireOp",EDGE,"E54.1");var subQ9=sQuery(id+"F3.wireOp",EDGE,"E54.0");var subQ10=sQuery(id+"F3.wireOp",EDGE,"E53");var subQ11=sQuery(id+"F3.wireOp",EDGE,"E52");var subQ12=sQuery(id+"F3.wireOp",EDGE,"E51");var subQ13=sQuery(id+"F3.wireOp",EDGE,"E50");var subQ14=sQuery(id+"F3.wireOp",EDGE,"E49");var subQ15=sQuery(id+"F3.wireOp",EDGE,"E48");var subQ16=sQuery(id+"F3.wireOp",EDGE,"E47");var subQ17=sQuery(id+"F3.wireOp",EDGE,"E46");var subQ18=sQuery(id+"F3.wireOp",EDGE,"E45");var subQ19=sQuery(id+"F3.wireOp",EDGE,"E44");Q0=makeQuery(id+"F18.boolean.opBoolean","MERGE",FACE,{"derivedFrom":[makeQuery(id+"F9.boolean.opBoolean","MERGE",FACE,{"derivedFrom":[makeQuery(id+"F8.opExtrude","CAP_FACE",FACE,{"disambiguationData":[OSD([subQ19,subQ18,subQ17,subQ16,subQ15,subQ14,subQ13,subQ12,subQ11,subQ10,subQ9,subQ8,subQ7,subQ6,subQ5,subQ4,subQ3,subQ2,subQ1,subQ0])],"isStart":false}),makeQuery(id+"F9.opExtrude","CAP_FACE",FACE,{"disambiguationData":[OSD([subQ19,subQ18,subQ17,subQ16,subQ15,subQ14,subQ13,subQ12,subQ11,subQ10,subQ9,subQ8,subQ7,subQ6,subQ5,subQ4,subQ3,subQ2,subQ1,subQ0])],"isStart":false})]}),makeQuery(id+"F18.opExtrude","CAP_FACE",FACE,{"disambiguationData":[OSD([subQ19,subQ18,subQ17,subQ16,subQ15,subQ14,subQ13,subQ12,subQ11,subQ10,subQ9,subQ8,subQ7,subQ6,subQ5,subQ4,subQ3,subQ2,subQ1,subQ0])],"isStart":false})]});}
            var sketch = newSketch(context, id + "F24", { "sketchPlane" : qUnion([Q0])});
            skCircle(sketch, "E80", {"center": v(-13.25, -36.55) * mm, "radius": 8.25 * mm, "construction": true});
            skCircle(sketch, "E81.MirrorC", {"center": v(13.25, -36.55) * mm, "radius": 8.25 * mm, "construction": true});
            skCircle(sketch, "E82", {"center": v(-13.25, -36.55) * mm, "radius": 3.25 * mm});
            skCircle(sketch, "E83", {"center": v(13.25, -36.55) * mm, "radius": 3.25 * mm});
            skLineSegment(sketch, "E84.0", {"start": v(19.3, 36.8) * mm, "end": v(-19.3, 36.8) * mm, "construction": true});
            skLineSegment(sketch, "E85.0", {"start": v(19.3, 36.8) * mm, "end": v(19.3, -45.3) * mm, "construction": true});
            skLineSegment(sketch, "E86.0", {"start": v(-19.3, -45.3) * mm, "end": v(-19.3, 36.8) * mm, "construction": true});
            skLineSegment(sketch, "E87", {"start": v(-19.3, -25.2) * mm, "end": v(19.3, -25.2) * mm, "construction": true});
            skLineSegment(sketch, "E88.bottom", {"start": v(-19.3, -25.2) * mm, "end": v(-9.3, -25.2) * mm});
            skLineSegment(sketch, "E88.top", {"start": v(-19.3, -27.2) * mm, "end": v(-9.3, -27.2) * mm});
            skLineSegment(sketch, "E88.left", {"start": v(-19.3, -25.2) * mm, "end": v(-19.3, -27.2) * mm});
            skLineSegment(sketch, "E88.right", {"start": v(-9.3, -25.2) * mm, "end": v(-9.3, -27.2) * mm});
            skLineSegment(sketch, "E89.MirrorCS", {"start": v(19.3, -27.2) * mm, "end": v(9.3, -27.2) * mm});
            skLineSegment(sketch, "E90.MirrorCS", {"start": v(9.3, -25.2) * mm, "end": v(9.3, -27.2) * mm});
            skLineSegment(sketch, "E91.MirrorCS", {"start": v(19.3, -25.2) * mm, "end": v(19.3, -27.2) * mm});
            skLineSegment(sketch, "E92.MirrorCS", {"start": v(19.3, -25.2) * mm, "end": v(9.3, -25.2) * mm});
            skSolve(sketch);
        }
        {
            var Q0;
            Q0=makeQuery(id+"F24.imprint","IMPRINT",FACE,{"disambiguationData":[TD([[makeQuery(id+"F24.imprint","IMPRINT",EDGE,{"derivedFrom":sQuery(id+"F24.wireOp",EDGE,"E82")}),1.0]])]});
            var Q1;
            Q1=makeQuery(id+"F24.imprint","IMPRINT",FACE,{"disambiguationData":[TD([[makeQuery(id+"F24.imprint","IMPRINT",EDGE,{"derivedFrom":sQuery(id+"F24.wireOp",EDGE,"E83")}),1.0]])]});
            var Q2;
            Q2=makeQuery(id+"F24.imprint","IMPRINT",FACE,{"disambiguationData":[TD([[makeQuery(id+"F24.imprint","IMPRINT",EDGE,{"derivedFrom":sQuery(id+"F24.wireOp",EDGE,"E88.bottom")}),-1.0]])]});
            var Q3;
            Q3=makeQuery(id+"F24.imprint","IMPRINT",FACE,{"disambiguationData":[TD([[makeQuery(id+"F24.imprint","IMPRINT",EDGE,{"derivedFrom":sQuery(id+"F24.wireOp",EDGE,"E90.MirrorCS")}),1.0]])]});
            extrude(context, id + "F25", {"entities" : qUnion([Q0, Q1, Q2, Q3]), "operationType" : NewBodyOperationType.ADD, "oppositeDirection" : true, "depth" : 10 * mm});
        }
        {
            var Q0;
            Q0=makeQuery(id+"F25.boolean.opBoolean","INTERSECT",EDGE,{"derivedFrom":[makeQuery(id+"F18.opExtrude","CAP_FACE",FACE,{"disambiguationData":[OSD([sQuery(id+"F3.wireOp",EDGE,"E44"),sQuery(id+"F3.wireOp",EDGE,"E45"),sQuery(id+"F3.wireOp",EDGE,"E46"),sQuery(id+"F3.wireOp",EDGE,"E47"),sQuery(id+"F3.wireOp",EDGE,"E48"),sQuery(id+"F3.wireOp",EDGE,"E49"),sQuery(id+"F3.wireOp",EDGE,"E50"),sQuery(id+"F3.wireOp",EDGE,"E51"),sQuery(id+"F3.wireOp",EDGE,"E52"),sQuery(id+"F3.wireOp",EDGE,"E53")])],"isStart":true}),makeQuery(id+"F25.opExtrude","SWEPT_FACE",FACE,{"disambiguationData":[OSD([sQuery(id+"F24.wireOp",EDGE,"E82")])]})]});
            var Q1;
            Q1=makeQuery(id+"F25.boolean.opBoolean","INTERSECT",EDGE,{"derivedFrom":[makeQuery(id+"F18.opExtrude","CAP_FACE",FACE,{"disambiguationData":[OSD([sQuery(id+"F3.wireOp",EDGE,"E44"),sQuery(id+"F3.wireOp",EDGE,"E45"),sQuery(id+"F3.wireOp",EDGE,"E46"),sQuery(id+"F3.wireOp",EDGE,"E47"),sQuery(id+"F3.wireOp",EDGE,"E48"),sQuery(id+"F3.wireOp",EDGE,"E49"),sQuery(id+"F3.wireOp",EDGE,"E50"),sQuery(id+"F3.wireOp",EDGE,"E51"),sQuery(id+"F3.wireOp",EDGE,"E52"),sQuery(id+"F3.wireOp",EDGE,"E53")])],"isStart":true}),makeQuery(id+"F25.opExtrude","SWEPT_FACE",FACE,{"disambiguationData":[OSD([sQuery(id+"F24.wireOp",EDGE,"E83")])]})]});
            var Q2;
            Q2=makeQuery(id+"F25.boolean.opBoolean","INTERSECT",EDGE,{"derivedFrom":[makeQuery(id+"F18.opExtrude","CAP_FACE",FACE,{"disambiguationData":[OSD([sQuery(id+"F3.wireOp",EDGE,"E44"),sQuery(id+"F3.wireOp",EDGE,"E45"),sQuery(id+"F3.wireOp",EDGE,"E46"),sQuery(id+"F3.wireOp",EDGE,"E47"),sQuery(id+"F3.wireOp",EDGE,"E48"),sQuery(id+"F3.wireOp",EDGE,"E49"),sQuery(id+"F3.wireOp",EDGE,"E50"),sQuery(id+"F3.wireOp",EDGE,"E51"),sQuery(id+"F3.wireOp",EDGE,"E52"),sQuery(id+"F3.wireOp",EDGE,"E53")])],"isStart":true}),makeQuery(id+"F25.opExtrude","SWEPT_FACE",FACE,{"disambiguationData":[OSD([sQuery(id+"F24.wireOp",EDGE,"E88.top")])]})]});
            var Q3;
            Q3=makeQuery(id+"F25.boolean.opBoolean","INTERSECT",EDGE,{"derivedFrom":[makeQuery(id+"F18.opExtrude","CAP_FACE",FACE,{"disambiguationData":[OSD([sQuery(id+"F3.wireOp",EDGE,"E44"),sQuery(id+"F3.wireOp",EDGE,"E45"),sQuery(id+"F3.wireOp",EDGE,"E46"),sQuery(id+"F3.wireOp",EDGE,"E47"),sQuery(id+"F3.wireOp",EDGE,"E48"),sQuery(id+"F3.wireOp",EDGE,"E49"),sQuery(id+"F3.wireOp",EDGE,"E50"),sQuery(id+"F3.wireOp",EDGE,"E51"),sQuery(id+"F3.wireOp",EDGE,"E52"),sQuery(id+"F3.wireOp",EDGE,"E53")])],"isStart":true}),makeQuery(id+"F25.opExtrude","SWEPT_FACE",FACE,{"disambiguationData":[OSD([sQuery(id+"F24.wireOp",EDGE,"E89.MirrorCS")])]})]});
            var Q4;
            Q4=makeQuery(id+"F25.opExtrude","SWEPT_EDGE",EDGE,{"disambiguationData":[OSD([sQuery(id+"F24.wireOp",EDGE,"E91.MirrorCS"),sQuery(id+"F24.wireOp",EDGE,"E89.MirrorCS")])]});
            var Q5;
            Q5=makeQuery(id+"F25.opExtrude","SWEPT_EDGE",EDGE,{"disambiguationData":[OSD([sQuery(id+"F24.wireOp",EDGE,"E88.top"),sQuery(id+"F24.wireOp",EDGE,"E88.left")])]});
            var Q6;
            Q6=makeQuery(id+"F18.boolean.opBoolean","INTERSECT",EDGE,{"derivedFrom":[makeQuery(id+"F9.opExtrude","SWEPT_FACE",FACE,{"disambiguationData":[OSD([sQuery(id+"F3.wireOp",EDGE,"E57")])]}),makeQuery(id+"F18.opExtrude","CAP_FACE",FACE,{"disambiguationData":[OSD([sQuery(id+"F3.wireOp",EDGE,"E44"),sQuery(id+"F3.wireOp",EDGE,"E45"),sQuery(id+"F3.wireOp",EDGE,"E46"),sQuery(id+"F3.wireOp",EDGE,"E47"),sQuery(id+"F3.wireOp",EDGE,"E48"),sQuery(id+"F3.wireOp",EDGE,"E49"),sQuery(id+"F3.wireOp",EDGE,"E50"),sQuery(id+"F3.wireOp",EDGE,"E51"),sQuery(id+"F3.wireOp",EDGE,"E52"),sQuery(id+"F3.wireOp",EDGE,"E53")])],"isStart":true})]});
            chamfer(context, id + "F26", {"entities" : qUnion([Q0, Q1, Q2, Q3, Q4, Q5, Q6]), "width" : 3 * mm, "tangentPropagation" : true});
        }
        {
            var Q0;
            Q0=sQuery(id+"F24.wireOp",VERTEX,"E80.center");
            var Q1;
            Q1=sQuery(id+"F24.wireOp",VERTEX,"E81.MirrorC.center");
            var Q2;
            Q2=makeQuery(id+"F8.opExtrude","SWEPT_BODY",BODY,{"disambiguationData":[OSD([sQuery(id+"F3.wireOp",EDGE,"E44"),sQuery(id+"F3.wireOp",EDGE,"E45"),sQuery(id+"F3.wireOp",EDGE,"E46"),sQuery(id+"F3.wireOp",EDGE,"E47"),sQuery(id+"F3.wireOp",EDGE,"E48"),sQuery(id+"F3.wireOp",EDGE,"E49"),sQuery(id+"F3.wireOp",EDGE,"E50"),sQuery(id+"F3.wireOp",EDGE,"E51"),sQuery(id+"F3.wireOp",EDGE,"E52"),sQuery(id+"F3.wireOp",EDGE,"E53"),sQuery(id+"F3.wireOp",EDGE,"E54.0"),sQuery(id+"F3.wireOp",EDGE,"E54.1"),sQuery(id+"F3.wireOp",EDGE,"E54.2"),sQuery(id+"F3.wireOp",EDGE,"E54.3"),sQuery(id+"F3.wireOp",EDGE,"E54.4"),sQuery(id+"F3.wireOp",EDGE,"E54.5"),sQuery(id+"F3.wireOp",EDGE,"E54.6"),sQuery(id+"F3.wireOp",EDGE,"E54.7"),sQuery(id+"F3.wireOp",EDGE,"E54.8"),sQuery(id+"F3.wireOp",EDGE,"E54.9")])]});
            hole(context, id + "F27", {"style" : HoleStyle.SIMPLE, "endStyle" : HoleEndStyle.THROUGH, "holeDiameter" : 2.4 * mm, "locations" : qUnion([Q0, Q1]), "scope" : qUnion([Q2]), "isTappedThrough" : true});
        }
        {
            var Q0;
            Q0=makeQuery(id+"F8.opExtrude","SWEPT_EDGE",EDGE,{"disambiguationData":[OSD([sQuery(id+"F3.wireOp",EDGE,"E54.7"),sQuery(id+"F3.wireOp",EDGE,"E54.8")])]});
            var Q1;
            Q1=makeQuery(id+"F8.opExtrude","SWEPT_EDGE",EDGE,{"disambiguationData":[OSD([sQuery(id+"F3.wireOp",EDGE,"E54.8"),sQuery(id+"F3.wireOp",EDGE,"E54.9")])]});
            fillet(context, id + "F28", {"entities" : qUnion([Q0, Q1]), "radius" : 3 * mm, "tangentPropagation" : true, "allowEdgeOverflow" : false});
        }
        {
            var Q0;
            Q0=makeQuery(id+"F7.boolean.opBoolean","COPY",EDGE,{"derivedFrom":makeQuery(id+"F7.opExtrude","SWEPT_EDGE",EDGE,{"disambiguationData":[OSD([sQuery(id+"F3.wireOp",EDGE,"E54.8"),sQuery(id+"F3.wireOp",EDGE,"E54.9")])]})});
            var Q1;
            Q1=makeQuery(id+"F7.boolean.opBoolean","COPY",EDGE,{"derivedFrom":makeQuery(id+"F7.opExtrude","SWEPT_EDGE",EDGE,{"disambiguationData":[OSD([sQuery(id+"F3.wireOp",EDGE,"E54.7"),sQuery(id+"F3.wireOp",EDGE,"E54.8")])]})});
            fillet(context, id + "F29", {"entities" : qUnion([Q0, Q1]), "radius" : 3.2 * mm, "tangentPropagation" : true, "allowEdgeOverflow" : false});
        }
        {
            var Q0;
            Q0=makeQuery(id+"F8.opExtrude","SWEPT_EDGE",EDGE,{"disambiguationData":[OSD([sQuery(id+"F3.wireOp",EDGE,"E45"),sQuery(id+"F3.wireOp",EDGE,"E46")])]});
            var Q1;
            Q1=makeQuery(id+"F6.opExtrude","SWEPT_EDGE",EDGE,{"disambiguationData":[OSD([sQuery(id+"F3.wireOp",EDGE,"E45"),sQuery(id+"F3.wireOp",EDGE,"E46")])]});
            var Q2;
            Q2=makeQuery(id+"F8.opExtrude","SWEPT_EDGE",EDGE,{"disambiguationData":[OSD([sQuery(id+"F3.wireOp",EDGE,"E45"),sQuery(id+"F3.wireOp",EDGE,"E51")])]});
            var Q3;
            Q3=makeQuery(id+"F6.opExtrude","SWEPT_EDGE",EDGE,{"disambiguationData":[OSD([sQuery(id+"F3.wireOp",EDGE,"E45"),sQuery(id+"F3.wireOp",EDGE,"E51")])]});
            var Q4;
            Q4=makeQuery(id+"F6.opExtrude","SWEPT_EDGE",EDGE,{"disambiguationData":[OSD([sQuery(id+"F3.wireOp",EDGE,"E49"),sQuery(id+"F3.wireOp",EDGE,"E51")])]});
            var Q5;
            Q5=makeQuery(id+"F6.opExtrude","SWEPT_EDGE",EDGE,{"disambiguationData":[OSD([sQuery(id+"F3.wireOp",EDGE,"E49"),sQuery(id+"F3.wireOp",EDGE,"E53")])]});
            var Q6;
            Q6=makeQuery(id+"F8.opExtrude","SWEPT_EDGE",EDGE,{"disambiguationData":[OSD([sQuery(id+"F3.wireOp",EDGE,"E49"),sQuery(id+"F3.wireOp",EDGE,"E51")])]});
            var Q7;
            Q7=makeQuery(id+"F8.opExtrude","SWEPT_EDGE",EDGE,{"disambiguationData":[OSD([sQuery(id+"F3.wireOp",EDGE,"E49"),sQuery(id+"F3.wireOp",EDGE,"E53")])]});
            var Q8;
            Q8=makeQuery(id+"F6.opExtrude","SWEPT_EDGE",EDGE,{"disambiguationData":[OSD([sQuery(id+"F3.wireOp",EDGE,"E44"),sQuery(id+"F3.wireOp",EDGE,"E46")])]});
            var Q9;
            Q9=makeQuery(id+"F6.opExtrude","SWEPT_EDGE",EDGE,{"disambiguationData":[OSD([sQuery(id+"F3.wireOp",EDGE,"E44"),sQuery(id+"F3.wireOp",EDGE,"E48")])]});
            var Q10;
            Q10=makeQuery(id+"F8.opExtrude","SWEPT_EDGE",EDGE,{"disambiguationData":[OSD([sQuery(id+"F3.wireOp",EDGE,"E47"),sQuery(id+"F3.wireOp",EDGE,"E48")])]});
            var Q11;
            Q11=makeQuery(id+"F6.opExtrude","SWEPT_EDGE",EDGE,{"disambiguationData":[OSD([sQuery(id+"F3.wireOp",EDGE,"E47"),sQuery(id+"F3.wireOp",EDGE,"E48")])]});
            var Q12;
            Q12=makeQuery(id+"F6.opExtrude","SWEPT_EDGE",EDGE,{"disambiguationData":[OSD([sQuery(id+"F3.wireOp",EDGE,"E47"),sQuery(id+"F3.wireOp",EDGE,"E52")])]});
            var Q13;
            Q13=makeQuery(id+"F8.opExtrude","SWEPT_EDGE",EDGE,{"disambiguationData":[OSD([sQuery(id+"F3.wireOp",EDGE,"E47"),sQuery(id+"F3.wireOp",EDGE,"E52")])]});
            var Q14;
            Q14=makeQuery(id+"F8.opExtrude","SWEPT_EDGE",EDGE,{"disambiguationData":[OSD([sQuery(id+"F3.wireOp",EDGE,"E50"),sQuery(id+"F3.wireOp",EDGE,"E52")])]});
            var Q15;
            Q15=makeQuery(id+"F6.opExtrude","SWEPT_EDGE",EDGE,{"disambiguationData":[OSD([sQuery(id+"F3.wireOp",EDGE,"E50"),sQuery(id+"F3.wireOp",EDGE,"E52")])]});
            var Q16;
            Q16=makeQuery(id+"F6.opExtrude","SWEPT_EDGE",EDGE,{"disambiguationData":[OSD([sQuery(id+"F3.wireOp",EDGE,"E50"),sQuery(id+"F3.wireOp",EDGE,"E53")])]});
            var Q17;
            Q17=makeQuery(id+"F8.opExtrude","SWEPT_EDGE",EDGE,{"disambiguationData":[OSD([sQuery(id+"F3.wireOp",EDGE,"E50"),sQuery(id+"F3.wireOp",EDGE,"E53")])]});
            var Q18;
            Q18=makeQuery(id+"F8.opExtrude","SWEPT_EDGE",EDGE,{"disambiguationData":[OSD([sQuery(id+"F3.wireOp",EDGE,"E44"),sQuery(id+"F3.wireOp",EDGE,"E48")])]});
            var Q19;
            Q19=makeQuery(id+"F8.opExtrude","SWEPT_EDGE",EDGE,{"disambiguationData":[OSD([sQuery(id+"F3.wireOp",EDGE,"E44"),sQuery(id+"F3.wireOp",EDGE,"E46")])]});
            fillet(context, id + "F30", {"entities" : qUnion([Q0, Q1, Q2, Q3, Q4, Q5, Q6, Q7, Q8, Q9, Q10, Q11, Q12, Q13, Q14, Q15, Q16, Q17, Q18, Q19]), "radius" : 5 * mm, "tangentPropagation" : true, "allowEdgeOverflow" : false});
        }
        {
            var Q0;
            Q0=makeQuery(id+"F16.boolean.opBoolean","COPY",FACE,{"derivedFrom":makeQuery(id+"F16.opExtrude","SWEPT_FACE",FACE,{"disambiguationData":[OSD([sQuery(id+"F4.wireOp",EDGE,"E62.MirrorCS")])]})});
            var Q1;
            Q1=makeQuery(id+"F16.boolean.opBoolean","COPY",FACE,{"derivedFrom":makeQuery(id+"F16.opExtrude","SWEPT_FACE",FACE,{"disambiguationData":[OSD([sQuery(id+"F4.wireOp",EDGE,"E59.top")])]})});
            var Q2;
            Q2=makeQuery(id+"F6.opExtrude","SWEPT_BODY",BODY,{"disambiguationData":[OSD([sQuery(id+"F3.wireOp",EDGE,"E44"),sQuery(id+"F3.wireOp",EDGE,"E45"),sQuery(id+"F3.wireOp",EDGE,"E46"),sQuery(id+"F3.wireOp",EDGE,"E47"),sQuery(id+"F3.wireOp",EDGE,"E48"),sQuery(id+"F3.wireOp",EDGE,"E49"),sQuery(id+"F3.wireOp",EDGE,"E50"),sQuery(id+"F3.wireOp",EDGE,"E51"),sQuery(id+"F3.wireOp",EDGE,"E52"),sQuery(id+"F3.wireOp",EDGE,"E53")])]});
            extrude(context, id + "F31", {"entities" : qUnion([Q0, Q1]), "operationType" : NewBodyOperationType.ADD, "endBound" : BoundingType.UP_TO_BODY, "endBoundEntityBody" : qUnion([Q2]), "depth" : 25 * mm, "hasSecondDirection" : true, "secondDirectionOppositeDirection" : false, "secondDirectionDepth" : 7 * mm});
        }
    });
